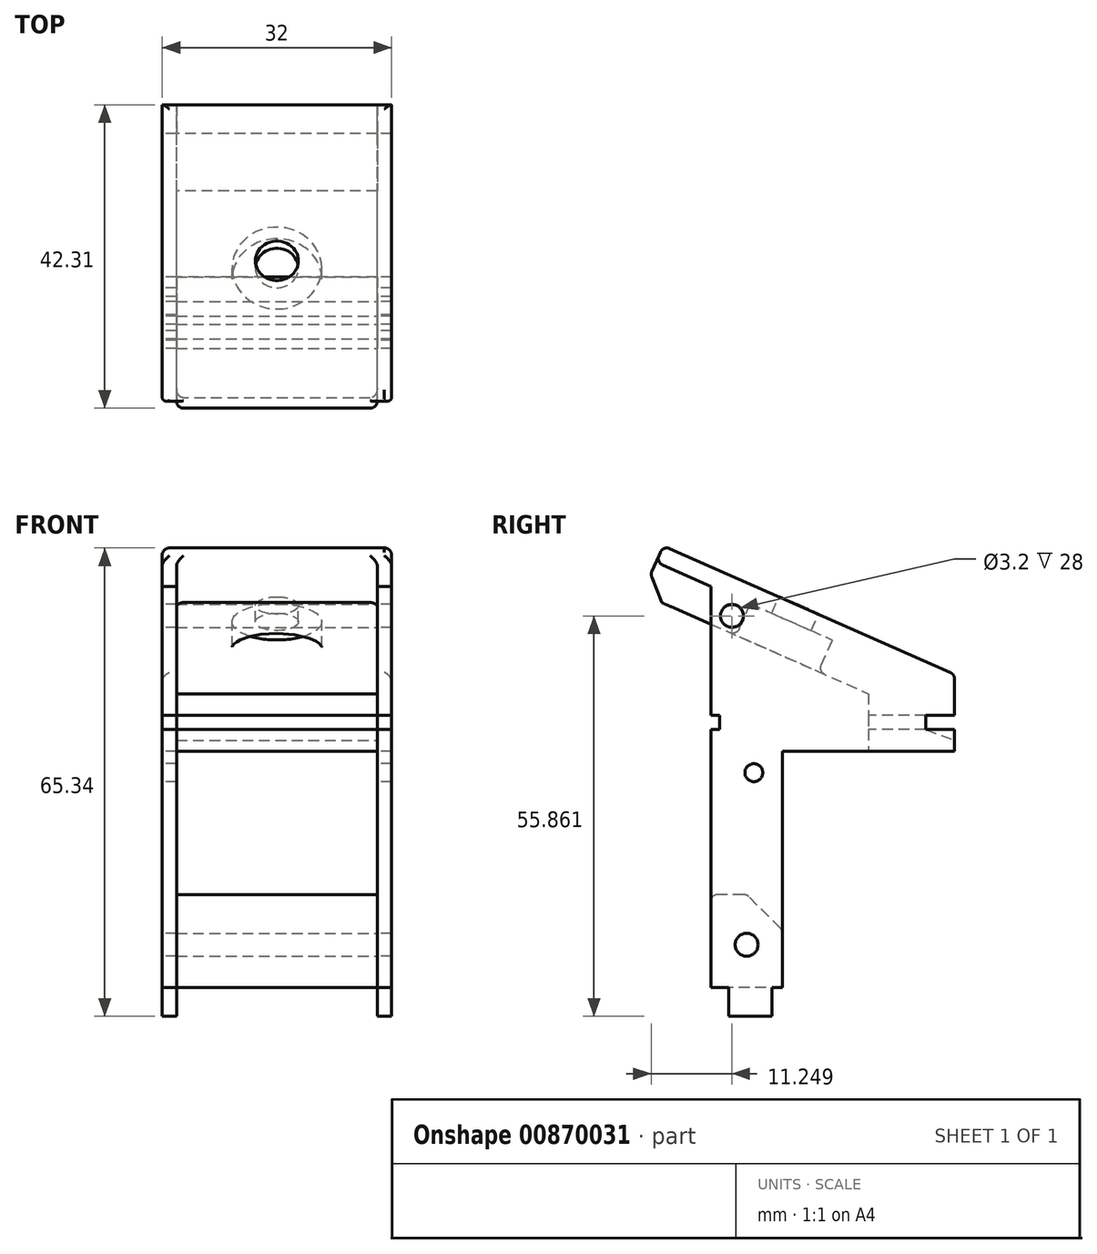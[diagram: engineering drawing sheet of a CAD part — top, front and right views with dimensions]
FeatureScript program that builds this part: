
annotation { "Feature Type Name" : "Feature", "Feature Type Description" : "" }
export const myFeature = defineFeature(function(context is Context, id is Id, definition is map)
    precondition{}
    {
        {
            var Q0;
            Q0=qCreatedBy(makeId("Right.planeOp"),FACE);
            var sketch = newSketch(context, id + "F0", { "sketchPlane" : qUnion([Q0])});
            skPoint(sketch, "E0.middle", {"position": v(0, 0) * mm});
            skLineSegment(sketch, "E1.top", {"start": v(-14.5, -23) * mm, "end": v(-8.5, -23) * mm});
            skLineSegment(sketch, "E1.left", {"start": v(-14.5, -19) * mm, "end": v(-14.5, -19) * mm});
            skLineSegment(sketch, "E2", {"start": v(-14.5, -19) * mm, "end": v(-14.5, -23) * mm});
            skLineSegment(sketch, "E3", {"start": v(-17, -19) * mm, "end": v(-14.5, -19) * mm});
            skLineSegment(sketch, "E4", {"start": v(-8.5, -23) * mm, "end": v(-8.5, -19) * mm});
            skLineSegment(sketch, "E5", {"start": v(13, 19) * mm, "end": v(13, 17) * mm});
            skLineSegment(sketch, "E6", {"start": v(13, 17) * mm, "end": v(17, 17) * mm});
            skLineSegment(sketch, "E7", {"start": v(17, 17) * mm, "end": v(17, 14) * mm});
            skLineSegment(sketch, "E8", {"start": v(17, 19) * mm, "end": v(17, 22) * mm});
            skLineSegment(sketch, "E9", {"start": v(13, 19) * mm, "end": v(17, 19) * mm});
            skLineSegment(sketch, "E10", {"start": v(-7, -19) * mm, "end": v(-7, 14) * mm});
            skLineSegment(sketch, "E11", {"start": v(-7, 14) * mm, "end": v(17, 14) * mm});
            skLineSegment(sketch, "E12", {"start": v(-8.5, -19) * mm, "end": v(-7, -19) * mm});
            skCircle(sketch, "E13", {"center": v(-11, 11) * mm, "radius": 1.25 * mm});
            skLineSegment(sketch, "E14", {"start": v(-17, 22) * mm, "end": v(17, 22) * mm});
            skLineSegment(sketch, "E15", {"start": v(-17, 22) * mm, "end": v(-17, 37) * mm});
            skLineSegment(sketch, "E16", {"start": v(-17, 37) * mm, "end": v(17, 22) * mm});
            skCircle(sketch, "E17", {"center": v(-14.05, 32.87) * mm, "radius": 1.6 * mm});
            skLineSegment(sketch, "E18", {"start": v(-17, 17) * mm, "end": v(-15.8, 17) * mm});
            skLineSegment(sketch, "E19", {"start": v(-15.8, 17) * mm, "end": v(-15.8, 19) * mm});
            skLineSegment(sketch, "E20", {"start": v(-15.8, 19) * mm, "end": v(-17, 19) * mm});
            skLineSegment(sketch, "E21", {"start": v(-17, 22) * mm, "end": v(-17, 19) * mm});
            skLineSegment(sketch, "E22", {"start": v(-17, 17) * mm, "end": v(-17, -19) * mm});
            skCircle(sketch, "E23", {"center": v(-12, -13) * mm, "radius": 1.6 * mm});
            skSolve(sketch);
        }
        {
            var Q0;
            Q0=makeQuery(id+"F0.imprint","IMPRINT",FACE,{"disambiguationData":[TD([[makeQuery(id+"F0.imprint","IMPRINT",EDGE,{"derivedFrom":sQuery(id+"F0.wireOp",EDGE,"E14")}),1.0]])]});
            var Q1;
            Q1=makeQuery(id+"F0.imprint","IMPRINT",FACE,{"disambiguationData":[TD([[makeQuery(id+"F0.imprint","IMPRINT",EDGE,{"derivedFrom":sQuery(id+"F0.wireOp",EDGE,"E1.top")}),1.0]])]});
            var Q2;
            Q2=makeQuery(id+"F0.imprint","IMPRINT",FACE,{"disambiguationData":[TD([[makeQuery(id+"F0.imprint","IMPRINT",EDGE,{"derivedFrom":sQuery(id+"F0.wireOp",EDGE,"xo18k5j8-xpip-QmOB-Rx07-EX14dvkylwDi.bottom")}),1.0]])]});
            extrude(context, id + "F1", {"entities" : qUnion([Q0, Q1, Q2]), "depth" : 2 * mm, "offsetDistance" : 25 * mm});
        }
        {
            var Q0;
            Q0=qCreatedBy(makeId("Top.planeOp"),FACE);
            var sketch = newSketch(context, id + "F2", { "sketchPlane" : qUnion([Q0])});
            skLineSegment(sketch, "E24.bottom", {"start": v(0, -17) * mm, "end": v(-30, -17) * mm, "construction": true});
            skLineSegment(sketch, "E24.top", {"start": v(0, 17) * mm, "end": v(-30, 17) * mm, "construction": true});
            skLineSegment(sketch, "E24.left", {"start": v(0, -17) * mm, "end": v(0, 17) * mm, "construction": true});
            skLineSegment(sketch, "E24.right", {"start": v(-30, -17) * mm, "end": v(-30, 17) * mm, "construction": true});
            skSolve(sketch);
        }
        {
            var Q0;
            Q0=makeQuery(id+"F1.opExtrude","SWEPT_BODY",BODY,{"disambiguationData":[OSD([sQuery(id+"F0.wireOp",EDGE,"E1.top"),sQuery(id+"F0.wireOp",EDGE,"E2"),sQuery(id+"F0.wireOp",EDGE,"E3"),sQuery(id+"F0.wireOp",EDGE,"FUvtoCSq-tBsc-r3IZ-kvKA-0zfOwn4Ue39q"),sQuery(id+"F0.wireOp",EDGE,"E4"),sQuery(id+"F0.wireOp",EDGE,"E5"),sQuery(id+"F0.wireOp",EDGE,"E6"),sQuery(id+"F0.wireOp",EDGE,"E7"),sQuery(id+"F0.wireOp",EDGE,"E8"),sQuery(id+"F0.wireOp",EDGE,"E9"),sQuery(id+"F0.wireOp",EDGE,"F9Ouq1Kr-n79l-Svws-RqGS-tpxa5rsozvrw"),sQuery(id+"F0.wireOp",EDGE,"E10"),sQuery(id+"F0.wireOp",EDGE,"E11"),sQuery(id+"F0.wireOp",EDGE,"E12"),sQuery(id+"F0.wireOp",EDGE,"E13"),sQuery(id+"F0.wireOp",EDGE,"E14")])]});
            var Q1;
            Q1=sQuery(id+"F2.wireOp",EDGE,"E24.bottom");
            transform(context, id + "F3", {"entities" : qUnion([Q0]), "transformType" : TransformType.TRANSLATION_ENTITY, "oppositeDirectionEntity" : false, "transformLine" : qUnion([Q1]), "makeCopy" : true});
        }
        {
            var Q0;
            Q0=makeQuery(id+"F3.opPattern","COPY",FACE,{"derivedFrom":makeQuery(id+"F1.opExtrude","SWEPT_FACE",FACE,{"disambiguationData":[OSD([sQuery(id+"F0.wireOp",EDGE,"E11")])]}),"instanceName":"1"});
            var sketch = newSketch(context, id + "F4", { "sketchPlane" : qUnion([Q0])});
            skLineSegment(sketch, "E25", {"start": v(0, -5) * mm, "end": v(-28, -5) * mm});
            skLineSegment(sketch, "E26.0", {"start": v(0, -17) * mm, "end": v(-28, -17) * mm});
            skLineSegment(sketch, "E27", {"start": v(0, -17) * mm, "end": v(0, -5) * mm});
            skLineSegment(sketch, "E28", {"start": v(-28, -17) * mm, "end": v(-28, -5) * mm});
            skSolve(sketch);
        }
        {
            var Q0;
            Q0 = qSketchRegion(id + "F4", true);
            extrude(context, id + "F5", {"entities" : qUnion([Q0]), "oppositeDirection" : true, "depth" : 3 * mm, "offsetDistance" : 25 * mm});
        }
        {
            var Q0;
            Q0=makeQuery(id+"F5.opExtrude","CAP_FACE",FACE,{"disambiguationData":[OSD([sQuery(id+"F4.wireOp",EDGE,"E25"),sQuery(id+"F4.wireOp",EDGE,"E26.0"),sQuery(id+"F4.wireOp",EDGE,"E27"),sQuery(id+"F4.wireOp",EDGE,"E28")])],"isStart":false});
            var sketch = newSketch(context, id + "F6", { "sketchPlane" : qUnion([Q0])});
            skLineSegment(sketch, "E29", {"start": v(-28, 13) * mm, "end": v(0, 13) * mm});
            skLineSegment(sketch, "E30.0", {"start": v(-28, 5) * mm, "end": v(0, 5) * mm});
            skLineSegment(sketch, "E31", {"start": v(-28, 5) * mm, "end": v(-28, 13) * mm});
            skLineSegment(sketch, "E32", {"start": v(0, 5) * mm, "end": v(0, 13) * mm});
            skSolve(sketch);
        }
        {
            var Q0;
            Q0=makeQuery(id+"F6.imprint","IMPRINT",FACE,{"disambiguationData":[TD([[makeQuery(id+"F6.imprint","IMPRINT",EDGE,{"derivedFrom":sQuery(id+"F6.wireOp",EDGE,"E29")}),-1.0]])]});
            extrude(context, id + "F7", {"entities" : qUnion([Q0]), "depth" : 2 * mm, "offsetDistance" : 25 * mm});
        }
        {
            var Q0;
            Q0=makeQuery(id+"F5.opExtrude","SWEPT_BODY",BODY,{"disambiguationData":[OSD([sQuery(id+"F4.wireOp",EDGE,"E25"),sQuery(id+"F4.wireOp",EDGE,"E26.0"),sQuery(id+"F4.wireOp",EDGE,"E27"),sQuery(id+"F4.wireOp",EDGE,"E28")])]});
            var Q1;
            Q1=qCreatedBy(makeId("Top.planeOp"),FACE);
            transform(context, id + "F8", {"entities" : qUnion([Q0]), "transformType" : TransformType.TRANSLATION_DISTANCE, "transformDirection" : qUnion([Q1]), "distance" : 5 * mm, "makeCopy" : true});
        }
        {
            var Q0;
            Q0=makeQuery(id+"F1.opExtrude","SWEPT_FACE",FACE,{"disambiguationData":[OSD([sQuery(id+"F0.wireOp",EDGE,"E15"),sQuery(id+"F0.wireOp",EDGE,"0SVESnR2-1dOJ-ite4-UzEn-XwyRMh8ifJJI")])]});
            var sketch = newSketch(context, id + "F9", { "sketchPlane" : qUnion([Q0])});
            skLineSegment(sketch, "E33.bottom", {"start": v(-28, -19) * mm, "end": v(0, -19) * mm});
            skLineSegment(sketch, "E33.top", {"start": v(-28, -6) * mm, "end": v(0, -6) * mm});
            skLineSegment(sketch, "E33.left", {"start": v(-28, -19) * mm, "end": v(-28, -6) * mm});
            skLineSegment(sketch, "E33.right", {"start": v(0, -19) * mm, "end": v(0, -6) * mm});
            skSolve(sketch);
        }
        {
            var Q0;
            Q0 = qSketchRegion(id + "F9", true);
            extrude(context, id + "F10", {"entities" : qUnion([Q0]), "oppositeDirection" : true, "depth" : 10 * mm, "offsetDistance" : 25 * mm});
        }
        {
            var Q0;
            Q0=qCreatedBy(makeId("Right.planeOp"),FACE);
            var sketch = newSketch(context, id + "F11", { "sketchPlane" : qUnion([Q0])});
            skLineSegment(sketch, "E34.0", {"start": v(17, 22) * mm, "end": v(5, 22) * mm});
            skLineSegment(sketch, "E35", {"start": v(-26.6, 35.94) * mm, "end": v(-24.65, 40.38) * mm});
            skLineSegment(sketch, "E36", {"start": v(17, 24.73) * mm, "end": v(17, 22) * mm});
            skLineSegment(sketch, "E37", {"start": v(-24.65, 40.38) * mm, "end": v(-23.64, 42.66) * mm});
            skCircle(sketch, "E38", {"center": v(-14.06, 32.86) * mm, "radius": 1.6 * mm});
            skLineSegment(sketch, "E39", {"start": v(-23.64, 42.66) * mm, "end": v(17, 24.73) * mm});
            skLineSegment(sketch, "E40", {"start": v(-24.65, 40.38) * mm, "end": v(17, 22) * mm});
            skLineSegment(sketch, "E41", {"start": v(-26.6, 35.94) * mm, "end": v(5, 22) * mm});
            skSolve(sketch);
        }
        {
            var Q0;
            Q0=makeQuery(id+"F11.imprint","IMPRINT",FACE,{"disambiguationData":[TD([[makeQuery(id+"F11.imprint","IMPRINT",EDGE,{"derivedFrom":sQuery(id+"F11.wireOp",EDGE,"E34.0")}),-1.0]])]});
            extrude(context, id + "F12", {"entities" : qUnion([Q0]), "oppositeDirection" : true, "depth" : 28 * mm, "offsetDistance" : 25 * mm});
        }
        {
            var Q0;
            Q0=makeQuery(id+"F11.imprint","IMPRINT",FACE,{"disambiguationData":[TD([[makeQuery(id+"F11.imprint","IMPRINT",EDGE,{"derivedFrom":sQuery(id+"F11.wireOp",EDGE,"pDA0NGMT-FcPk-uskz-Uwn8-zbtIRN8ivZcj")}),1.0]])]});
            var Q1;
            Q1=makeQuery(id+"F11.imprint","IMPRINT",FACE,{"disambiguationData":[TD([[makeQuery(id+"F11.imprint","IMPRINT",EDGE,{"derivedFrom":sQuery(id+"F11.wireOp",EDGE,"E36")}),-1.0]])]});
            extrude(context, id + "F13", {"entities" : qUnion([Q0, Q1]), "operationType" : NewBodyOperationType.ADD, "oppositeDirection" : true, "depth" : 30 * mm, "offsetDistance" : 25 * mm, "hasSecondDirection" : true, "secondDirectionOppositeDirection" : false, "secondDirectionDepth" : 2 * mm});
        }
        {
            var Q0;
            Q0=makeQuery(id+"F12.opExtrude","SWEPT_EDGE",EDGE,{"disambiguationData":[OSD([sQuery(id+"F11.wireOp",EDGE,"E35"),sQuery(id+"F11.wireOp",EDGE,"JGb2U0d4-BEP0-3rHj-2fiR-yxyYSapYEOGi")])]});
            chamfer(context, id + "F14", {"entities" : qUnion([Q0]), "width" : 3 * mm, "tangentPropagation" : true});
        }
        {
            var Q0;
            Q0=makeQuery(id+"F13.opExtrude","CAP_EDGE",EDGE,{"disambiguationData":[OSD([sQuery(id+"F11.wireOp",EDGE,"dqufNdB6-NSFh-Uecf-0olV-1ydPr70zTpyi")])],"isStart":true});
            var Q1;
            Q1=makeQuery(id+"F13.opExtrude","CAP_EDGE",EDGE,{"disambiguationData":[OSD([sQuery(id+"F11.wireOp",EDGE,"dqufNdB6-NSFh-Uecf-0olV-1ydPr70zTpyi")])],"isStart":false});
            var Q2;
            Q2=makeQuery(id+"F13.opExtrude","SWEPT_EDGE",EDGE,{"disambiguationData":[OSD([sQuery(id+"F11.wireOp",EDGE,"a706aae3-896c-4f0a-8dbf-968627393644.0"),sQuery(id+"F11.wireOp",EDGE,"E37")])]});
            var Q3;
            {var subQ0=sQuery(id+"F11.wireOp",EDGE,"E35");Q3=makeQuery(id+"F14.opChamfer","BLEND_EDGE",EDGE,{"blendedFrom":[makeQuery(id+"F12.opExtrude","SWEPT_EDGE",EDGE,{"disambiguationData":[OSD([subQ0,sQuery(id+"F11.wireOp",EDGE,"JGb2U0d4-BEP0-3rHj-2fiR-yxyYSapYEOGi")])]}),makeQuery(id+"F13.boolean.opBoolean","MERGE",FACE,{"derivedFrom":[makeQuery(id+"F12.opExtrude","SWEPT_FACE",FACE,{"disambiguationData":[OSD([subQ0])]}),makeQuery(id+"F13.opExtrude","SWEPT_FACE",FACE,{"disambiguationData":[OSD([sQuery(id+"F11.wireOp",EDGE,"E37")])]})]})],"blendedInto":[makeQuery(id+"F13.boolean.opBoolean","MERGE",FACE,{"derivedFrom":[makeQuery(id+"F12.opExtrude","SWEPT_FACE",FACE,{"disambiguationData":[OSD([subQ0])]}),makeQuery(id+"F13.opExtrude","SWEPT_FACE",FACE,{"disambiguationData":[OSD([sQuery(id+"F11.wireOp",EDGE,"E37")])]})]})]});}
            var Q4;
            {var subQ0=sQuery(id+"F11.wireOp",EDGE,"JGb2U0d4-BEP0-3rHj-2fiR-yxyYSapYEOGi");Q4=makeQuery(id+"F14.opChamfer","BLEND_EDGE",EDGE,{"blendedFrom":[makeQuery(id+"F12.opExtrude","SWEPT_EDGE",EDGE,{"disambiguationData":[OSD([sQuery(id+"F11.wireOp",EDGE,"E35"),subQ0])]}),makeQuery(id+"F12.opExtrude","SWEPT_FACE",FACE,{"disambiguationData":[OSD([sQuery(id+"F11.wireOp",EDGE,"4oYtStz3-3Ugv-912H-aIS9-75qggSmpGT8C"),subQ0])]})],"blendedInto":[makeQuery(id+"F12.opExtrude","SWEPT_FACE",FACE,{"disambiguationData":[OSD([sQuery(id+"F11.wireOp",EDGE,"4oYtStz3-3Ugv-912H-aIS9-75qggSmpGT8C"),subQ0])]})]});}
            var Q5;
            {var subQ0=sQuery(id+"F11.wireOp",EDGE,"JGb2U0d4-BEP0-3rHj-2fiR-yxyYSapYEOGi");var subQ1=sQuery(id+"F11.wireOp",EDGE,"E35");Q5=makeQuery(id+"F14.opChamfer","BLEND_EDGE",EDGE,{"blendedFrom":[makeQuery(id+"F12.opExtrude","SWEPT_EDGE",EDGE,{"disambiguationData":[OSD([subQ1,subQ0])]}),makeQuery(id+"F12.opExtrude","CAP_FACE",FACE,{"disambiguationData":[OSD([sQuery(id+"F11.wireOp",EDGE,"E34.0"),sQuery(id+"F11.wireOp",EDGE,"pDA0NGMT-FcPk-uskz-Uwn8-zbtIRN8ivZcj"),sQuery(id+"F11.wireOp",EDGE,"4oYtStz3-3Ugv-912H-aIS9-75qggSmpGT8C"),subQ1,sQuery(id+"F11.wireOp",EDGE,"LekVqZk1-XtwK-oY0d-L2o3-87X4Kr4PufJ1"),subQ0])],"isStart":false})],"blendedInto":[makeQuery(id+"F12.opExtrude","CAP_FACE",FACE,{"disambiguationData":[OSD([sQuery(id+"F11.wireOp",EDGE,"E34.0"),sQuery(id+"F11.wireOp",EDGE,"pDA0NGMT-FcPk-uskz-Uwn8-zbtIRN8ivZcj"),sQuery(id+"F11.wireOp",EDGE,"4oYtStz3-3Ugv-912H-aIS9-75qggSmpGT8C"),subQ1,sQuery(id+"F11.wireOp",EDGE,"LekVqZk1-XtwK-oY0d-L2o3-87X4Kr4PufJ1"),subQ0])],"isStart":false})]});}
            var Q6;
            {var subQ0=sQuery(id+"F11.wireOp",EDGE,"JGb2U0d4-BEP0-3rHj-2fiR-yxyYSapYEOGi");var subQ1=sQuery(id+"F11.wireOp",EDGE,"E35");Q6=makeQuery(id+"F14.opChamfer","BLEND_EDGE",EDGE,{"blendedFrom":[makeQuery(id+"F12.opExtrude","SWEPT_EDGE",EDGE,{"disambiguationData":[OSD([subQ1,subQ0])]}),makeQuery(id+"F12.opExtrude","CAP_FACE",FACE,{"disambiguationData":[OSD([sQuery(id+"F11.wireOp",EDGE,"E34.0"),sQuery(id+"F11.wireOp",EDGE,"pDA0NGMT-FcPk-uskz-Uwn8-zbtIRN8ivZcj"),sQuery(id+"F11.wireOp",EDGE,"4oYtStz3-3Ugv-912H-aIS9-75qggSmpGT8C"),subQ1,sQuery(id+"F11.wireOp",EDGE,"LekVqZk1-XtwK-oY0d-L2o3-87X4Kr4PufJ1"),subQ0])],"isStart":true})],"blendedInto":[makeQuery(id+"F12.opExtrude","CAP_FACE",FACE,{"disambiguationData":[OSD([sQuery(id+"F11.wireOp",EDGE,"E34.0"),sQuery(id+"F11.wireOp",EDGE,"pDA0NGMT-FcPk-uskz-Uwn8-zbtIRN8ivZcj"),sQuery(id+"F11.wireOp",EDGE,"4oYtStz3-3Ugv-912H-aIS9-75qggSmpGT8C"),subQ1,sQuery(id+"F11.wireOp",EDGE,"LekVqZk1-XtwK-oY0d-L2o3-87X4Kr4PufJ1"),subQ0])],"isStart":true})]});}
            var Q7;
            {var subQ0=sQuery(id+"F11.wireOp",EDGE,"LekVqZk1-XtwK-oY0d-L2o3-87X4Kr4PufJ1");var subQ1=sQuery(id+"F11.wireOp",EDGE,"E37");var subQ2=sQuery(id+"F11.wireOp",EDGE,"pDA0NGMT-FcPk-uskz-Uwn8-zbtIRN8ivZcj");var subQ3=sQuery(id+"F11.wireOp",EDGE,"E35");Q7=makeQuery(id+"F13.boolean.opBoolean","SPLIT",EDGE,{"disambiguationData":[TD([makeQuery(id+"F12.opExtrude","CAP_FACE",FACE,{"disambiguationData":[OSD([sQuery(id+"F11.wireOp",EDGE,"E34.0"),subQ2,sQuery(id+"F11.wireOp",EDGE,"4oYtStz3-3Ugv-912H-aIS9-75qggSmpGT8C"),subQ3,subQ0,sQuery(id+"F11.wireOp",EDGE,"JGb2U0d4-BEP0-3rHj-2fiR-yxyYSapYEOGi")])],"isStart":false})])],"derivedFrom":makeQuery(id+"F13.opExtrude","SWEPT_EDGE",EDGE,{"disambiguationData":[OSD([subQ3,subQ0,subQ1])]})});}
            var Q8;
            {var subQ0=sQuery(id+"F11.wireOp",EDGE,"LekVqZk1-XtwK-oY0d-L2o3-87X4Kr4PufJ1");var subQ1=sQuery(id+"F11.wireOp",EDGE,"E37");var subQ2=sQuery(id+"F11.wireOp",EDGE,"pDA0NGMT-FcPk-uskz-Uwn8-zbtIRN8ivZcj");var subQ3=sQuery(id+"F11.wireOp",EDGE,"E35");Q8=makeQuery(id+"F13.boolean.opBoolean","SPLIT",EDGE,{"disambiguationData":[TD([makeQuery(id+"F12.opExtrude","CAP_FACE",FACE,{"disambiguationData":[OSD([sQuery(id+"F11.wireOp",EDGE,"E34.0"),subQ2,sQuery(id+"F11.wireOp",EDGE,"4oYtStz3-3Ugv-912H-aIS9-75qggSmpGT8C"),subQ3,subQ0,sQuery(id+"F11.wireOp",EDGE,"JGb2U0d4-BEP0-3rHj-2fiR-yxyYSapYEOGi")])],"isStart":true})])],"derivedFrom":makeQuery(id+"F13.opExtrude","SWEPT_EDGE",EDGE,{"disambiguationData":[OSD([subQ3,subQ0,subQ1])]})});}
            var Q9;
            Q9=makeQuery(id+"F13.opExtrude","CAP_EDGE",EDGE,{"disambiguationData":[OSD([sQuery(id+"F11.wireOp",EDGE,"E37")])],"isStart":false});
            var Q10;
            Q10=makeQuery(id+"F13.opExtrude","CAP_EDGE",EDGE,{"disambiguationData":[OSD([sQuery(id+"F11.wireOp",EDGE,"E37")])],"isStart":true});
            var Q11;
            Q11=makeQuery(id+"F12.opExtrude","CAP_EDGE",EDGE,{"disambiguationData":[OSD([sQuery(id+"F11.wireOp",EDGE,"E35")])],"isStart":false});
            var Q12;
            Q12=makeQuery(id+"F12.opExtrude","CAP_EDGE",EDGE,{"disambiguationData":[OSD([sQuery(id+"F11.wireOp",EDGE,"E35")])],"isStart":true});
            var Q13;
            Q13=makeQuery(id+"F13.opExtrude","CAP_EDGE",EDGE,{"disambiguationData":[OSD([sQuery(id+"F11.wireOp",EDGE,"a706aae3-896c-4f0a-8dbf-968627393644.0")])],"isStart":true});
            var Q14;
            Q14=makeQuery(id+"F13.opExtrude","SWEPT_EDGE",EDGE,{"disambiguationData":[OSD([sQuery(id+"F11.wireOp",EDGE,"a706aae3-896c-4f0a-8dbf-968627393644.0"),sQuery(id+"F11.wireOp",EDGE,"E37")])]});
            var Q15;
            {var subQ0=sQuery(id+"F11.wireOp",EDGE,"E35");Q15=makeQuery(id+"F14.opChamfer","BLEND_EDGE",EDGE,{"blendedFrom":[makeQuery(id+"F12.opExtrude","SWEPT_EDGE",EDGE,{"disambiguationData":[OSD([subQ0,sQuery(id+"F11.wireOp",EDGE,"JGb2U0d4-BEP0-3rHj-2fiR-yxyYSapYEOGi")])]}),makeQuery(id+"F13.boolean.opBoolean","MERGE",FACE,{"derivedFrom":[makeQuery(id+"F12.opExtrude","SWEPT_FACE",FACE,{"disambiguationData":[OSD([subQ0])]}),makeQuery(id+"F13.opExtrude","SWEPT_FACE",FACE,{"disambiguationData":[OSD([sQuery(id+"F11.wireOp",EDGE,"E37")])]})]})],"blendedInto":[makeQuery(id+"F13.boolean.opBoolean","MERGE",FACE,{"derivedFrom":[makeQuery(id+"F12.opExtrude","SWEPT_FACE",FACE,{"disambiguationData":[OSD([subQ0])]}),makeQuery(id+"F13.opExtrude","SWEPT_FACE",FACE,{"disambiguationData":[OSD([sQuery(id+"F11.wireOp",EDGE,"E37")])]})]})]});}
            var Q16;
            Q16=makeQuery(id+"F12.opExtrude","CAP_EDGE",EDGE,{"disambiguationData":[OSD([sQuery(id+"F11.wireOp",EDGE,"E35")])],"isStart":false});
            var Q17;
            {var subQ0=sQuery(id+"F11.wireOp",EDGE,"LekVqZk1-XtwK-oY0d-L2o3-87X4Kr4PufJ1");var subQ1=sQuery(id+"F11.wireOp",EDGE,"E37");var subQ2=sQuery(id+"F11.wireOp",EDGE,"pDA0NGMT-FcPk-uskz-Uwn8-zbtIRN8ivZcj");var subQ3=sQuery(id+"F11.wireOp",EDGE,"E35");Q17=makeQuery(id+"F13.boolean.opBoolean","SPLIT",EDGE,{"disambiguationData":[TD([makeQuery(id+"F12.opExtrude","CAP_FACE",FACE,{"disambiguationData":[OSD([sQuery(id+"F11.wireOp",EDGE,"E34.0"),subQ2,sQuery(id+"F11.wireOp",EDGE,"4oYtStz3-3Ugv-912H-aIS9-75qggSmpGT8C"),subQ3,subQ0,sQuery(id+"F11.wireOp",EDGE,"JGb2U0d4-BEP0-3rHj-2fiR-yxyYSapYEOGi")])],"isStart":false})])],"derivedFrom":makeQuery(id+"F13.opExtrude","SWEPT_EDGE",EDGE,{"disambiguationData":[OSD([subQ3,subQ0,subQ1])]})});}
            var Q18;
            Q18=makeQuery(id+"F13.opExtrude","CAP_EDGE",EDGE,{"disambiguationData":[OSD([sQuery(id+"F11.wireOp",EDGE,"E37")])],"isStart":false});
            var Q19;
            Q19=makeQuery(id+"F12.opExtrude","CAP_EDGE",EDGE,{"disambiguationData":[OSD([sQuery(id+"F11.wireOp",EDGE,"E35")])],"isStart":true});
            var Q20;
            {var subQ0=sQuery(id+"F11.wireOp",EDGE,"LekVqZk1-XtwK-oY0d-L2o3-87X4Kr4PufJ1");var subQ1=sQuery(id+"F11.wireOp",EDGE,"E37");var subQ2=sQuery(id+"F11.wireOp",EDGE,"pDA0NGMT-FcPk-uskz-Uwn8-zbtIRN8ivZcj");var subQ3=sQuery(id+"F11.wireOp",EDGE,"E35");Q20=makeQuery(id+"F13.boolean.opBoolean","SPLIT",EDGE,{"disambiguationData":[TD([makeQuery(id+"F12.opExtrude","CAP_FACE",FACE,{"disambiguationData":[OSD([sQuery(id+"F11.wireOp",EDGE,"E34.0"),subQ2,sQuery(id+"F11.wireOp",EDGE,"4oYtStz3-3Ugv-912H-aIS9-75qggSmpGT8C"),subQ3,subQ0,sQuery(id+"F11.wireOp",EDGE,"JGb2U0d4-BEP0-3rHj-2fiR-yxyYSapYEOGi")])],"isStart":true})])],"derivedFrom":makeQuery(id+"F13.opExtrude","SWEPT_EDGE",EDGE,{"disambiguationData":[OSD([subQ3,subQ0,subQ1])]})});}
            var Q21;
            Q21=makeQuery(id+"F13.opExtrude","CAP_EDGE",EDGE,{"disambiguationData":[OSD([sQuery(id+"F11.wireOp",EDGE,"E37")])],"isStart":true});
            var Q22;
            {var subQ0=sQuery(id+"F11.wireOp",EDGE,"JGb2U0d4-BEP0-3rHj-2fiR-yxyYSapYEOGi");var subQ1=sQuery(id+"F11.wireOp",EDGE,"E35");Q22=makeQuery(id+"F14.opChamfer","BLEND_EDGE",EDGE,{"blendedFrom":[makeQuery(id+"F12.opExtrude","SWEPT_EDGE",EDGE,{"disambiguationData":[OSD([subQ1,subQ0])]}),makeQuery(id+"F12.opExtrude","CAP_FACE",FACE,{"disambiguationData":[OSD([sQuery(id+"F11.wireOp",EDGE,"E34.0"),sQuery(id+"F11.wireOp",EDGE,"pDA0NGMT-FcPk-uskz-Uwn8-zbtIRN8ivZcj"),sQuery(id+"F11.wireOp",EDGE,"4oYtStz3-3Ugv-912H-aIS9-75qggSmpGT8C"),subQ1,sQuery(id+"F11.wireOp",EDGE,"LekVqZk1-XtwK-oY0d-L2o3-87X4Kr4PufJ1"),subQ0])],"isStart":false})],"blendedInto":[makeQuery(id+"F12.opExtrude","CAP_FACE",FACE,{"disambiguationData":[OSD([sQuery(id+"F11.wireOp",EDGE,"E34.0"),sQuery(id+"F11.wireOp",EDGE,"pDA0NGMT-FcPk-uskz-Uwn8-zbtIRN8ivZcj"),sQuery(id+"F11.wireOp",EDGE,"4oYtStz3-3Ugv-912H-aIS9-75qggSmpGT8C"),subQ1,sQuery(id+"F11.wireOp",EDGE,"LekVqZk1-XtwK-oY0d-L2o3-87X4Kr4PufJ1"),subQ0])],"isStart":false})]});}
            var Q23;
            {var subQ0=sQuery(id+"F11.wireOp",EDGE,"JGb2U0d4-BEP0-3rHj-2fiR-yxyYSapYEOGi");var subQ1=sQuery(id+"F11.wireOp",EDGE,"E35");Q23=makeQuery(id+"F14.opChamfer","BLEND_EDGE",EDGE,{"blendedFrom":[makeQuery(id+"F12.opExtrude","SWEPT_EDGE",EDGE,{"disambiguationData":[OSD([subQ1,subQ0])]}),makeQuery(id+"F12.opExtrude","CAP_FACE",FACE,{"disambiguationData":[OSD([sQuery(id+"F11.wireOp",EDGE,"E34.0"),sQuery(id+"F11.wireOp",EDGE,"pDA0NGMT-FcPk-uskz-Uwn8-zbtIRN8ivZcj"),sQuery(id+"F11.wireOp",EDGE,"4oYtStz3-3Ugv-912H-aIS9-75qggSmpGT8C"),subQ1,sQuery(id+"F11.wireOp",EDGE,"LekVqZk1-XtwK-oY0d-L2o3-87X4Kr4PufJ1"),subQ0])],"isStart":true})],"blendedInto":[makeQuery(id+"F12.opExtrude","CAP_FACE",FACE,{"disambiguationData":[OSD([sQuery(id+"F11.wireOp",EDGE,"E34.0"),sQuery(id+"F11.wireOp",EDGE,"pDA0NGMT-FcPk-uskz-Uwn8-zbtIRN8ivZcj"),sQuery(id+"F11.wireOp",EDGE,"4oYtStz3-3Ugv-912H-aIS9-75qggSmpGT8C"),subQ1,sQuery(id+"F11.wireOp",EDGE,"LekVqZk1-XtwK-oY0d-L2o3-87X4Kr4PufJ1"),subQ0])],"isStart":true})]});}
            var Q24;
            Q24=makeQuery(id+"F13.opExtrude","CAP_EDGE",EDGE,{"disambiguationData":[OSD([sQuery(id+"F11.wireOp",EDGE,"dqufNdB6-NSFh-Uecf-0olV-1ydPr70zTpyi")])],"isStart":false});
            var Q25;
            Q25=makeQuery(id+"F13.opExtrude","CAP_EDGE",EDGE,{"disambiguationData":[OSD([sQuery(id+"F11.wireOp",EDGE,"a706aae3-896c-4f0a-8dbf-968627393644.0")])],"isStart":false});
            var Q26;
            Q26=makeQuery(id+"F13.opExtrude","CAP_EDGE",EDGE,{"disambiguationData":[OSD([sQuery(id+"F11.wireOp",EDGE,"a706aae3-896c-4f0a-8dbf-968627393644.0")])],"isStart":true});
            var Q27;
            Q27=makeQuery(id+"F13.opExtrude","CAP_EDGE",EDGE,{"disambiguationData":[OSD([sQuery(id+"F11.wireOp",EDGE,"dqufNdB6-NSFh-Uecf-0olV-1ydPr70zTpyi")])],"isStart":true});
            var Q28;
            Q28=makeQuery(id+"F13.opExtrude","SWEPT_EDGE",EDGE,{"disambiguationData":[OSD([sQuery(id+"F11.wireOp",EDGE,"dqufNdB6-NSFh-Uecf-0olV-1ydPr70zTpyi"),sQuery(id+"F11.wireOp",EDGE,"E36")])]});
            var Q29;
            Q29=makeQuery(id+"F13.opExtrude","CAP_EDGE",EDGE,{"disambiguationData":[OSD([sQuery(id+"F11.wireOp",EDGE,"E39")])],"isStart":true});
            var Q30;
            Q30=makeQuery(id+"F13.opExtrude","CAP_EDGE",EDGE,{"disambiguationData":[OSD([sQuery(id+"F11.wireOp",EDGE,"E39")])],"isStart":false});
            fillet(context, id + "F15", {"entities" : qUnion([Q0, Q1, Q2, Q3, Q4, Q5, Q6, Q7, Q8, Q9, Q10, Q11, Q12, Q13, Q14, Q15, Q16, Q17, Q18, Q19, Q20, Q21, Q22, Q23, Q24, Q25, Q26, Q27, Q28, Q29, Q30]), "radius" : 1 * mm, "allowEdgeOverflow" : false});
        }
        {
            var Q0;
            Q0=makeQuery(id+"F13.opExtrude","SWEPT_FACE",FACE,{"disambiguationData":[OSD([sQuery(id+"F11.wireOp",EDGE,"E39")])]});
            var sketch = newSketch(context, id + "F16", { "sketchPlane" : qUnion([Q0])});
            skPoint(sketch, "E42.startSnap0", {"position": v(-14.1, -43.36) * mm});
            skCircle(sketch, "E43", {"center": v(-14, -18.2) * mm, "radius": 3 * mm});
            skCircle(sketch, "E44", {"center": v(-14, -18.2) * mm, "radius": 6.25 * mm});
            skSolve(sketch);
        }
        {
            var Q0;
            Q0 = qSketchRegion(id + "F16", true);
            var Q1;
            Q1=makeQuery(id+"F16.imprint","IMPRINT",FACE,{"disambiguationData":[TD([[makeQuery(id+"F16.imprint","IMPRINT",EDGE,{"derivedFrom":sQuery(id+"F16.wireOp",EDGE,"E43")}),1.0]])]});
            var Q2;
            Q2=makeQuery(id+"F16.imprint","IMPRINT",FACE,{"disambiguationData":[TD([[makeQuery(id+"F16.imprint","IMPRINT",EDGE,{"derivedFrom":sQuery(id+"F16.wireOp",EDGE,"E43")}),1.0]])]});
            var Q3;
            Q3=makeQuery(id+"F16.imprint","IMPRINT",FACE,{"disambiguationData":[TD([[makeQuery(id+"F16.imprint","IMPRINT",EDGE,{"derivedFrom":sQuery(id+"F16.wireOp",EDGE,"E43")}),1.0]])]});
            var Q4;
            Q4=makeQuery(id+"F16.imprint","IMPRINT",FACE,{"disambiguationData":[TD([[makeQuery(id+"F16.imprint","IMPRINT",EDGE,{"derivedFrom":sQuery(id+"F16.wireOp",EDGE,"E43")}),-1.0]])]});
            var Q5;
            Q5=makeQuery(id+"F16.imprint","IMPRINT",FACE,{"disambiguationData":[TD([[makeQuery(id+"F16.imprint","IMPRINT",EDGE,{"derivedFrom":sQuery(id+"F16.wireOp",EDGE,"E43")}),1.0]])]});
            extrude(context, id + "F17", {"entities" : qUnion([Q0, Q1, Q2, Q3, Q4, Q5]), "operationType" : NewBodyOperationType.REMOVE, "oppositeDirection" : true, "depth" : 10 * mm, "offsetDistance" : 25 * mm});
        }
        {
            var Q0;
            Q0=makeQuery(id+"F16.imprint","IMPRINT",FACE,{"disambiguationData":[TD([[makeQuery(id+"F16.imprint","IMPRINT",EDGE,{"derivedFrom":sQuery(id+"F16.wireOp",EDGE,"E43")}),-1.0]])]});
            extrude(context, id + "F18", {"entities" : qUnion([Q0]), "operationType" : NewBodyOperationType.ADD, "oppositeDirection" : true, "depth" : 2.5 * mm, "offsetDistance" : 25 * mm});
        }
        {
            var Q0;
            Q0=makeQuery(id+"F17.boolean.opBoolean","INTERSECT",EDGE,{"derivedFrom":[makeQuery(id+"F12.opExtrude","SWEPT_FACE",FACE,{"disambiguationData":[OSD([sQuery(id+"F11.wireOp",EDGE,"E41")])]}),makeQuery(id+"F17.opExtrude","SWEPT_FACE",FACE,{"disambiguationData":[OSD([sQuery(id+"F16.wireOp",EDGE,"E44")])]})]});
            fillet(context, id + "F19", {"entities" : qUnion([Q0]), "radius" : 1 * mm, "tangentPropagation" : true, "allowEdgeOverflow" : false});
        }
        {
            var Q0;
            Q0=makeQuery(id+"F5.opExtrude","CAP_EDGE",EDGE,{"disambiguationData":[OSD([sQuery(id+"F4.wireOp",EDGE,"E26.0")])],"isStart":false});
            chamfer(context, id + "F20", {"entities" : qUnion([Q0]), "chamferType" : ChamferType.TWO_OFFSETS, "width1" : 4 * mm, "oppositeDirection" : false, "width2" : 1.5 * mm, "tangentPropagation" : true});
        }
        {
            var Q0;
            Q0=makeQuery(id+"F0.imprint","IMPRINT",FACE,{"disambiguationData":[TD([[makeQuery(id+"F0.imprint","IMPRINT",EDGE,{"derivedFrom":sQuery(id+"F0.wireOp",EDGE,"E23")}),1.0]])]});
            extrude(context, id + "F21", {"entities" : qUnion([Q0]), "operationType" : NewBodyOperationType.REMOVE, "oppositeDirection" : true, "depth" : 28 * mm, "offsetDistance" : 25 * mm});
        }
        {
            var Q0;
            Q0=makeQuery(id+"F10.opExtrude","CAP_EDGE",EDGE,{"disambiguationData":[OSD([sQuery(id+"F9.wireOp",EDGE,"E33.top")])],"isStart":false});
            chamfer(context, id + "F22", {"entities" : qUnion([Q0]), "width" : 5 * mm, "tangentPropagation" : true});
        }
        {
            var Q0;
            Q0=makeQuery(id+"F10.opExtrude","CAP_EDGE",EDGE,{"disambiguationData":[OSD([sQuery(id+"F9.wireOp",EDGE,"E33.top")])],"isStart":true});
            var Q1;
            {var subQ0=sQuery(id+"F9.wireOp",EDGE,"E33.top");Q1=makeQuery(id+"F22.opChamfer","BLEND_EDGE",EDGE,{"blendedFrom":[makeQuery(id+"F10.opExtrude","CAP_EDGE",EDGE,{"disambiguationData":[OSD([subQ0])],"isStart":false}),makeQuery(id+"F10.opExtrude","SWEPT_FACE",FACE,{"disambiguationData":[OSD([subQ0])]})],"blendedInto":[makeQuery(id+"F10.opExtrude","SWEPT_FACE",FACE,{"disambiguationData":[OSD([subQ0])]})]});}
            var Q2;
            {var subQ0=sQuery(id+"F9.wireOp",EDGE,"E33.top");Q2=makeQuery(id+"F22.opChamfer","BLEND_EDGE",EDGE,{"blendedFrom":[makeQuery(id+"F10.opExtrude","CAP_EDGE",EDGE,{"disambiguationData":[OSD([subQ0])],"isStart":false}),makeQuery(id+"F10.opExtrude","CAP_FACE",FACE,{"disambiguationData":[OSD([sQuery(id+"F9.wireOp",EDGE,"E33.bottom"),subQ0,sQuery(id+"F9.wireOp",EDGE,"E33.left"),sQuery(id+"F9.wireOp",EDGE,"E33.right")])],"isStart":false})],"blendedInto":[makeQuery(id+"F10.opExtrude","CAP_FACE",FACE,{"disambiguationData":[OSD([sQuery(id+"F9.wireOp",EDGE,"E33.bottom"),subQ0,sQuery(id+"F9.wireOp",EDGE,"E33.left"),sQuery(id+"F9.wireOp",EDGE,"E33.right")])],"isStart":false})]});}
            fillet(context, id + "F23", {"entities" : qUnion([Q0, Q1, Q2]), "radius" : 1 * mm, "tangentPropagation" : true, "allowEdgeOverflow" : false});
        }
    });
